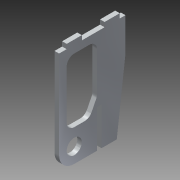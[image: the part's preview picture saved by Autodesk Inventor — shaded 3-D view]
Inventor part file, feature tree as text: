
AUTODESK INVENTOR PART (.ipt)
format: ipt  version: 2013 (Build 170138000, 138)  size: 148,480 bytes
history: native  units: mm
features: extrude x1, sketch x1
ambient origin geometry x8: Origin, YZ Plane, XZ Plane, XY Plane, X Axis, Y Axis, Z Axis, Center Point
feature tree (2):
  extrude  "Extrusion2"  Depth=10.0mm
  sketch  "Sketch1"  dims[d5=50.0mm d6=66.5mm d7=10.0mm d10=5.0mm d12=10.0mm d17=10.0mm d18=3.0mm d20=10.0mm d21=3.0mm d22=5.0mm d23=15.0mm d24=3.0mm d25=3.0mm d42=3.0mm d46=3.75mm d47=22.0mm d49=2.0mm d54=10.0mm d55=15.0mm d57=68.0mm d58=15.75mm d59=25.0mm d61=5.0mm d65=5.0mm d66=10.0mm d67=5.0mm d68=5.0mm d69=3.0mm d70=0.0mm]
